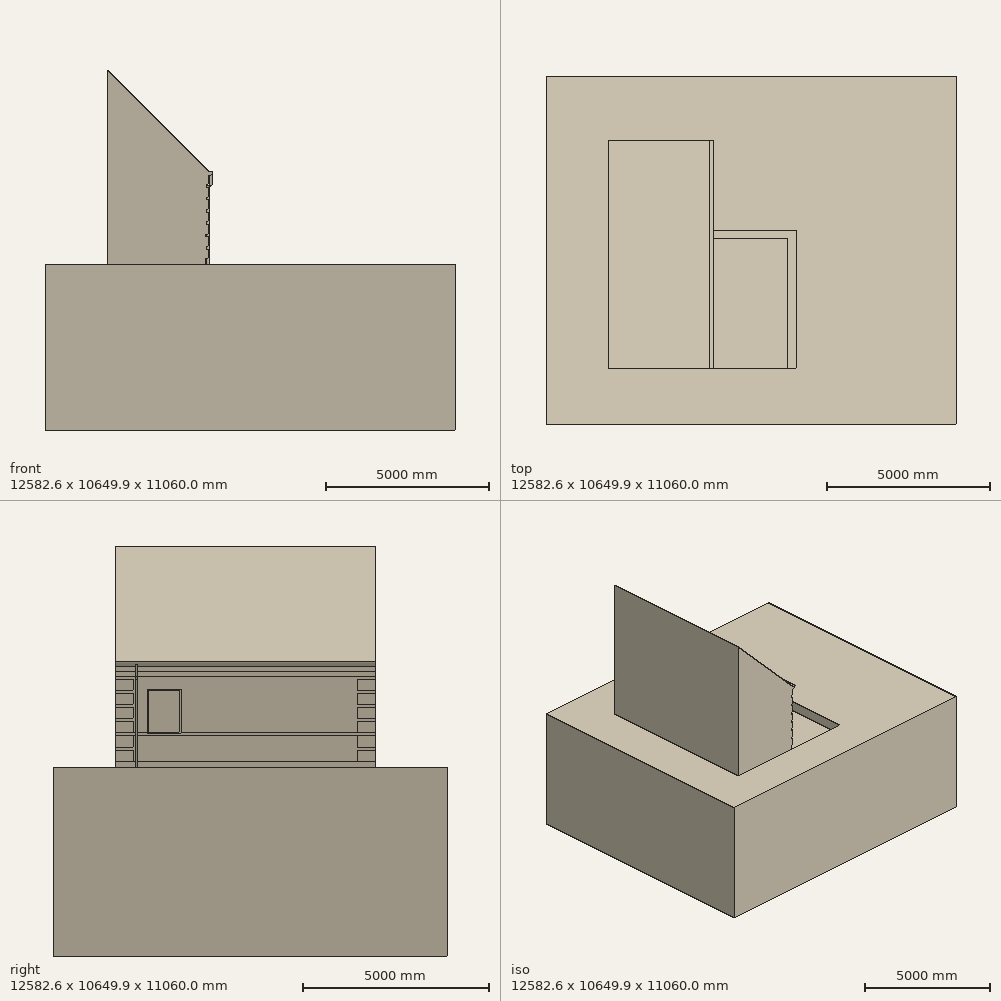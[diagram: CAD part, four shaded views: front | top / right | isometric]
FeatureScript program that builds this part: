
annotation { "Feature Type Name" : "Feature", "Feature Type Description" : "" }
export const myFeature = defineFeature(function(context is Context, id is Id, definition is map)
    precondition{}
    {
        {
            var Q0;
            Q0=qCreatedBy(makeId("Front.planeOp"),FACE);
            var sketch = newSketch(context, id + "F0", { "sketchPlane" : qUnion([Q0])});
            skLineSegment(sketch, "E0", {"start": v(80, 180) * mm, "end": v(80, 480) * mm});
            skLineSegment(sketch, "E1", {"start": v(80, 480) * mm, "end": v(40, 480) * mm});
            skLineSegment(sketch, "E2", {"start": v(40, 480) * mm, "end": v(40, 560) * mm});
            skLineSegment(sketch, "E3", {"start": v(40, 560) * mm, "end": v(80, 560) * mm});
            skLineSegment(sketch, "E4", {"start": v(80, 560) * mm, "end": v(80, 860) * mm});
            skLineSegment(sketch, "E5", {"start": v(80, 860) * mm, "end": v(10, 860) * mm});
            skLineSegment(sketch, "E6", {"start": v(10, 860) * mm, "end": v(10, 940) * mm});
            skLineSegment(sketch, "E7", {"start": v(10, 940) * mm, "end": v(80, 940) * mm});
            skLineSegment(sketch, "E8", {"start": v(80, 940) * mm, "end": v(80, 1240) * mm});
            skLineSegment(sketch, "E9", {"start": v(80, 1240) * mm, "end": v(40, 1240) * mm});
            skLineSegment(sketch, "E10", {"start": v(40, 1240) * mm, "end": v(40, 1320) * mm});
            skLineSegment(sketch, "E11", {"start": v(40, 1320) * mm, "end": v(80, 1320) * mm});
            skLineSegment(sketch, "E12", {"start": v(80, 1320) * mm, "end": v(80, 1620) * mm});
            skLineSegment(sketch, "E13", {"start": v(80, 1620) * mm, "end": v(40, 1620) * mm});
            skLineSegment(sketch, "E14", {"start": v(40, 1620) * mm, "end": v(40, 1700) * mm});
            skLineSegment(sketch, "E15", {"start": v(40, 1700) * mm, "end": v(80, 1700) * mm});
            skLineSegment(sketch, "E16", {"start": v(80, 1700) * mm, "end": v(80, 2000) * mm});
            skLineSegment(sketch, "E17", {"start": v(80, 2380) * mm, "end": v(40, 2380) * mm});
            skLineSegment(sketch, "E18", {"start": v(40, 2380) * mm, "end": v(40, 2460) * mm});
            skLineSegment(sketch, "E19", {"start": v(40, 2460) * mm, "end": v(80, 2460) * mm});
            skLineSegment(sketch, "E20", {"start": v(80, 2000) * mm, "end": v(40, 2000) * mm});
            skLineSegment(sketch, "E21", {"start": v(40, 2000) * mm, "end": v(40, 2080) * mm});
            skLineSegment(sketch, "E22", {"start": v(40, 2080) * mm, "end": v(80, 2080) * mm});
            skLineSegment(sketch, "E23", {"start": v(80, 2080) * mm, "end": v(80, 2380) * mm});
            skLineSegment(sketch, "E24", {"start": v(-3000, 0) * mm, "end": v(-3000, 5970) * mm});
            skLineSegment(sketch, "E25", {"start": v(80, 2460) * mm, "end": v(80, 2600) * mm});
            skLineSegment(sketch, "E26", {"start": v(80, 2600) * mm, "end": v(100, 2600) * mm});
            skLineSegment(sketch, "E27", {"start": v(100, 2600) * mm, "end": v(100, 2740) * mm});
            skLineSegment(sketch, "E28", {"start": v(100, 2740) * mm, "end": v(110, 2740) * mm});
            skLineSegment(sketch, "E29", {"start": v(230, 2860) * mm, "end": v(230, 2870) * mm});
            skLineSegment(sketch, "E30", {"start": v(230, 2870) * mm, "end": v(100, 2870) * mm});
            skPoint(sketch, "E31.visualSharp", {"position": v(230, 2740) * mm});
            skArc(sketch, "E31.filletArc", {"start": v(110, 2740) * mm, "mid": v(194.85, 2775.15) * mm, "end": v(230, 2860) * mm});
            skLineSegment(sketch, "E32", {"start": v(0, 0) * mm, "end": v(-3000, 0) * mm});
            skLineSegment(sketch, "E33", {"start": v(100, 2870) * mm, "end": v(-3000, 5970) * mm});
            skLineSegment(sketch, "E34", {"start": v(80, 180) * mm, "end": v(0, 180) * mm});
            skLineSegment(sketch, "E35", {"start": v(0, 180) * mm, "end": v(0, 0) * mm});
            skSolve(sketch);
        }
        {
            var Q0;
            Q0=makeQuery(id+"F0.imprint","IMPRINT",FACE,{"disambiguationData":[TD([[makeQuery(id+"F0.imprint","IMPRINT",EDGE,{"derivedFrom":sQuery(id+"F0.wireOp",EDGE,"6GGYYeqi-GWG1-YfQA-pEUI-Re84fh06RRRH")}),1.0]])]});
            var Q1;
            Q1=makeQuery(id+"F0.imprint","IMPRINT",FACE,{"disambiguationData":[TD([[makeQuery(id+"F0.imprint","IMPRINT",EDGE,{"derivedFrom":sQuery(id+"F0.wireOp",EDGE,"E0")}),1.0]])]});
            extrude(context, id + "F1", {"entities" : qUnion([Q0, Q1]), "oppositeDirection" : true, "depth" : 7000 * mm, "offsetDistance" : 25 * mm});
        }
        {
            var Q0;
            Q0=makeQuery(id+"F1.opExtrude","SWEPT_FACE",FACE,{"disambiguationData":[OSD([sQuery(id+"F0.wireOp",EDGE,"E23")])]});
            var sketch = newSketch(context, id + "F2", { "sketchPlane" : qUnion([Q0])});
            skLineSegment(sketch, "E36.bottom", {"start": v(480, 0) * mm, "end": v(6520, 0) * mm});
            skLineSegment(sketch, "E36.top", {"start": v(480, 2460) * mm, "end": v(6520, 2460) * mm});
            skLineSegment(sketch, "E36.left", {"start": v(480, 0) * mm, "end": v(480, 2460) * mm});
            skLineSegment(sketch, "E36.right", {"start": v(6520, 0) * mm, "end": v(6520, 2460) * mm});
            skSolve(sketch);
        }
        {
            var Q0;
            Q0 = qSketchRegion(id + "F2", true);
            var Q1;
            Q1=makeQuery(id+"F1.opExtrude","SWEPT_FACE",FACE,{"disambiguationData":[OSD([sQuery(id+"F0.wireOp",EDGE,"E21")])]});
            extrude(context, id + "F3", {"entities" : qUnion([Q0]), "operationType" : NewBodyOperationType.REMOVE, "endBound" : BoundingType.UP_TO_SURFACE, "oppositeDirection" : true, "depth" : 25 * mm, "endBoundEntityFace" : qUnion([Q1]), "offsetDistance" : 25 * mm});
        }
        {
            var Q0;
            Q0=makeQuery(id+"F3.boolean.opBoolean","COPY",FACE,{"disambiguationData":[TD([makeQuery(id+"F1.opExtrude","SWEPT_FACE",FACE,{"disambiguationData":[OSD([sQuery(id+"F0.wireOp",EDGE,"E17")])]})])],"derivedFrom":makeQuery(id+"F3.opExtrude","SWEPT_FACE",FACE,{"disambiguationData":[OSD([sQuery(id+"F2.wireOp",EDGE,"E36.left")])]})});
            cPlane(context, id + "F4", {"entities" : qUnion([Q0]), "cplaneType" : CPlaneType.OFFSET, "offset" : 75 * mm, "width" : 150 * mm, "height" : 150 * mm});
        }
        {
            var Q0;
            Q0=qCreatedBy(id+"F4.planeOp",FACE);
            var sketch = newSketch(context, id + "F5", { "sketchPlane" : qUnion([Q0])});
            skLineSegment(sketch, "E37", {"start": v(-165, 2870) * mm, "end": v(-165, 2450) * mm});
            skLineSegment(sketch, "E38", {"start": v(-125, 2410) * mm, "end": v(-120, 2410) * mm});
            skLineSegment(sketch, "E39", {"start": v(-80, 2370) * mm, "end": v(-80, 0) * mm});
            skPoint(sketch, "E40.visualSharp", {"position": v(-165, 2410) * mm});
            skArc(sketch, "E40.filletArc", {"start": v(-165, 2450) * mm, "mid": v(-153.28, 2421.72) * mm, "end": v(-125, 2410) * mm});
            skPoint(sketch, "E41.visualSharp", {"position": v(-80, 2410) * mm});
            skArc(sketch, "E41.filletArc", {"start": v(-80, 2370) * mm, "mid": v(-91.72, 2398.28) * mm, "end": v(-120, 2410) * mm});
            skSolve(sketch);
        }
        {
            var Q0;
            Q0=makeQuery(id+"F1.opExtrude","SWEPT_FACE",FACE,{"disambiguationData":[OSD([sQuery(id+"F0.wireOp",EDGE,"E32")])]});
            var sketch = newSketch(context, id + "F6", { "sketchPlane" : qUnion([Q0])});
            skCircle(sketch, "E42", {"center": v(80, -555) * mm, "radius": 37.5 * mm});
            skSolve(sketch);
        }
        {
            var Q0;
            Q0 = qSketchRegion(id + "F6", true);
            var Q1;
            Q1=sQuery(id+"F5.wireOp",EDGE,"E37");
            var Q2;
            Q2=sQuery(id+"F5.wireOp",EDGE,"E38");
            var Q3;
            Q3=sQuery(id+"F5.wireOp",EDGE,"E40.filletArc");
            var Q4;
            Q4=sQuery(id+"F5.wireOp",EDGE,"E41.filletArc");
            var Q5;
            Q5=sQuery(id+"F5.wireOp",EDGE,"E39");
            sweep(context, id + "F7", {"operationType" : NewBodyOperationType.ADD, "profiles" : qUnion([Q0]), "path" : qUnion([Q1, Q2, Q3, Q4, Q5])});
        }
        {
            var Q0;
            {var subQ0=sQuery(id+"F0.wireOp",EDGE,"E21");Q0=makeQuery(id+"F3.boolean.opBoolean","MERGE",FACE,{"derivedFrom":[makeQuery(id+"F1.opExtrude","SWEPT_FACE",FACE,{"disambiguationData":[OSD([sQuery(id+"F0.wireOp",EDGE,"E10")])]}),makeQuery(id+"F1.opExtrude","SWEPT_FACE",FACE,{"disambiguationData":[OSD([sQuery(id+"F0.wireOp",EDGE,"E14")])]}),makeQuery(id+"F1.opExtrude","SWEPT_FACE",FACE,{"disambiguationData":[OSD([sQuery(id+"F0.wireOp",EDGE,"E18")])]}),makeQuery(id+"F1.opExtrude","SWEPT_FACE",FACE,{"disambiguationData":[OSD([subQ0])]}),makeQuery(id+"F3.opExtrude","CAP_FACE",FACE,{"disambiguationData":[OSD([subQ0])],"isStart":false})]});}
            var sketch = newSketch(context, id + "F8", { "sketchPlane" : qUnion([Q0])});
            skLineSegment(sketch, "E43.bottom", {"start": v(1760, 2120) * mm, "end": v(850, 2120) * mm});
            skLineSegment(sketch, "E43.top", {"start": v(1760, 920) * mm, "end": v(850, 920) * mm});
            skLineSegment(sketch, "E43.left", {"start": v(1760, 2120) * mm, "end": v(1760, 920) * mm});
            skLineSegment(sketch, "E43.right", {"start": v(850, 2120) * mm, "end": v(850, 920) * mm});
            skPoint(sketch, "E43.middle", {"position": v(1305, 1520) * mm});
            skSolve(sketch);
        }
        {
            var Q0;
            Q0 = qSketchRegion(id + "F8", true);
            extrude(context, id + "F9", {"entities" : qUnion([Q0]), "operationType" : NewBodyOperationType.REMOVE, "oppositeDirection" : true, "depth" : 200 * mm, "offsetDistance" : 25 * mm});
        }
        {
            var Q0;
            Q0=makeQuery(id+"F9.boolean.opBoolean","COPY",FACE,{"derivedFrom":makeQuery(id+"F9.opExtrude","CAP_FACE",FACE,{"disambiguationData":[OSD([sQuery(id+"F8.wireOp",EDGE,"E43.bottom"),sQuery(id+"F8.wireOp",EDGE,"E43.top"),sQuery(id+"F8.wireOp",EDGE,"E43.left"),sQuery(id+"F8.wireOp",EDGE,"E43.right")])],"isStart":false})});
            var sketch = newSketch(context, id + "F10", { "sketchPlane" : qUnion([Q0])});
            skLineSegment(sketch, "E44.bottom", {"start": v(890, 2090) * mm, "end": v(1720, 2090) * mm});
            skLineSegment(sketch, "E44.top", {"start": v(890, 950) * mm, "end": v(1720, 950) * mm});
            skLineSegment(sketch, "E44.left", {"start": v(890, 2090) * mm, "end": v(890, 950) * mm});
            skLineSegment(sketch, "E44.right", {"start": v(1720, 2090) * mm, "end": v(1720, 950) * mm});
            skLineSegment(sketch, "E45", {"start": v(850, 920) * mm, "end": v(890, 950) * mm, "construction": true});
            skLineSegment(sketch, "E46", {"start": v(1720, 2090) * mm, "end": v(1760, 2120) * mm, "construction": true});
            skLineSegment(sketch, "E47", {"start": v(890, 950) * mm, "end": v(890, 920) * mm, "construction": true});
            skLineSegment(sketch, "E48", {"start": v(890, 950) * mm, "end": v(850, 950) * mm, "construction": true});
            skLineSegment(sketch, "E49", {"start": v(1720, 2090) * mm, "end": v(1720, 2120) * mm, "construction": true});
            skLineSegment(sketch, "E50", {"start": v(1720, 2090) * mm, "end": v(1760, 2090) * mm, "construction": true});
            skLineSegment(sketch, "E51", {"start": v(1305, 950) * mm, "end": v(1305, 2090) * mm, "construction": true});
            skPoint(sketch, "E52.middle", {"position": v(1092.5, 1893.33) * mm});
            skSolve(sketch);
        }
        {
            var Q0;
            Q0=makeQuery(id+"F10.imprint","IMPRINT",FACE,{"disambiguationData":[TD([[makeQuery(id+"F10.imprint","IMPRINT",EDGE,{"derivedFrom":sQuery(id+"F10.wireOp",EDGE,"E44.bottom")}),1.0]])]});
            extrude(context, id + "F11", {"entities" : qUnion([Q0]), "operationType" : NewBodyOperationType.ADD, "depth" : 150 * mm, "offsetDistance" : 25 * mm});
        }
        {
            var Q0;
            Q0=makeQuery(id+"F1.opExtrude","SWEPT_FACE",FACE,{"disambiguationData":[OSD([sQuery(id+"F0.wireOp",EDGE,"E32")])]});
            var sketch = newSketch(context, id + "F12", { "sketchPlane" : qUnion([Q0])});
            skLineSegment(sketch, "E53.bottom", {"start": v(-4907.83, 1693.97) * mm, "end": v(7674.74, 1693.97) * mm});
            skLineSegment(sketch, "E53.top", {"start": v(-4907.83, -8955.92) * mm, "end": v(7674.74, -8955.92) * mm});
            skLineSegment(sketch, "E53.left", {"start": v(-4907.83, 1693.97) * mm, "end": v(-4907.83, -8955.92) * mm});
            skLineSegment(sketch, "E53.right", {"start": v(7674.74, 1693.97) * mm, "end": v(7674.74, -8955.92) * mm});
            skSolve(sketch);
        }
        {
            var Q0;
            Q0=makeQuery(id+"F12.imprint","IMPRINT",FACE,{"disambiguationData":[TD([[makeQuery(id+"F12.imprint","IMPRINT",EDGE,{"derivedFrom":sQuery(id+"F12.wireOp",EDGE,"E53.bottom")}),-1.0]])]});
            var Q1;
            {var subQ0=sQuery(id+"F0.wireOp",EDGE,"E32");Q1=makeQuery(id+"F12.imprint","IMPRINT",FACE,{"disambiguationData":[TD([[makeQuery(id+"F12.imprint","IMPRINT",EDGE,{"derivedFrom":makeQuery(id+"F1.opExtrude","CAP_EDGE",EDGE,{"disambiguationData":[OSD([subQ0])],"isStart":true})}),1.0]])]});}
            extrude(context, id + "F13", {"entities" : qUnion([Q0, Q1]), "depth" : 5090 * mm, "offsetDistance" : 25 * mm});
        }
        {
            var Q0;
            Q0=makeQuery(id+"F13.opExtrude","CAP_FACE",FACE,{"disambiguationData":[OSD([sQuery(id+"F12.wireOp",EDGE,"E53.bottom"),sQuery(id+"F12.wireOp",EDGE,"E53.top"),sQuery(id+"F12.wireOp",EDGE,"E53.left"),sQuery(id+"F12.wireOp",EDGE,"E53.right")])],"isStart":true});
            var sketch = newSketch(context, id + "F14", { "sketchPlane" : qUnion([Q0])});
            skLineSegment(sketch, "E54.bottom", {"start": v(0, 0) * mm, "end": v(2500, 0) * mm});
            skLineSegment(sketch, "E54.top", {"start": v(0, 4000) * mm, "end": v(2500, 4000) * mm});
            skLineSegment(sketch, "E54.left", {"start": v(0, 0) * mm, "end": v(0, 4000) * mm});
            skLineSegment(sketch, "E54.right", {"start": v(2500, 0) * mm, "end": v(2500, 4000) * mm});
            skLineSegment(sketch, "E55.bottom", {"start": v(2500, 0) * mm, "end": v(2750, 0) * mm});
            skLineSegment(sketch, "E55.top", {"start": v(2500, 4250) * mm, "end": v(2750, 4250) * mm});
            skLineSegment(sketch, "E55.left", {"start": v(2500, 0) * mm, "end": v(2500, 4250) * mm});
            skLineSegment(sketch, "E55.right", {"start": v(2750, 0) * mm, "end": v(2750, 4250) * mm});
            skLineSegment(sketch, "E56.top", {"start": v(0, 4250) * mm, "end": v(2500, 4250) * mm});
            skLineSegment(sketch, "E56.left", {"start": v(0, 4000) * mm, "end": v(0, 4250) * mm});
            skLineSegment(sketch, "E56.right", {"start": v(2500, 4000) * mm, "end": v(2500, 4250) * mm});
            skSolve(sketch);
        }
        {
            var Q0;
            Q0=makeQuery(id+"F14.imprint","IMPRINT",FACE,{"disambiguationData":[TD([[makeQuery(id+"F14.imprint","IMPRINT",EDGE,{"derivedFrom":sQuery(id+"F14.wireOp",EDGE,"E54.bottom")}),1.0]])]});
            extrude(context, id + "F15", {"entities" : qUnion([Q0]), "operationType" : NewBodyOperationType.REMOVE, "oppositeDirection" : true, "depth" : 200 * mm, "offsetDistance" : 25 * mm});
        }
        {
            var Q0;
            Q0=makeQuery(id+"F14.imprint","IMPRINT",FACE,{"disambiguationData":[TD([[makeQuery(id+"F14.imprint","IMPRINT",EDGE,{"derivedFrom":sQuery(id+"F14.wireOp",EDGE,"E55.bottom")}),1.0]])]});
            var Q1;
            Q1=makeQuery(id+"F14.imprint","IMPRINT",FACE,{"disambiguationData":[TD([[makeQuery(id+"F14.imprint","IMPRINT",EDGE,{"derivedFrom":sQuery(id+"F14.wireOp",EDGE,"E54.top")}),1.0]])]});
            extrude(context, id + "F16", {"entities" : qUnion([Q0, Q1]), "operationType" : NewBodyOperationType.REMOVE, "oppositeDirection" : true, "depth" : 900 * mm, "offsetDistance" : 25 * mm});
        }
    });
